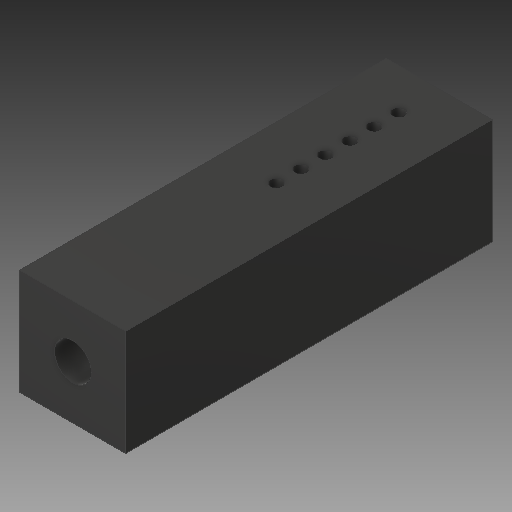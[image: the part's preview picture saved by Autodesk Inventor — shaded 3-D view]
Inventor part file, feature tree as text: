
AUTODESK INVENTOR PART (.ipt)
format: ipt  version: 2019 (Build 230136000, 136)  size: 146,432 bytes
history: native  units: mm
features: sketch x3, hole x2, extrude x1
ambient origin geometry x8: Origin, YZ Plane, XZ Plane, XY Plane, X Axis, Y Axis, Z Axis, Center Point
bodies: Solid1 (feature_tree)
feature tree (6):
  extrude  "Extrusion1"  Depth=13.0mm
  hole  "Hole1"  [1 undecoded]
  hole  "Hole2"  [1 undecoded]
  sketch  "Sketch1"  dims[d0=13.0mm d1=13.0mm]
  sketch  "Sketch2"  dims[d2=45.0mm d3=0.0mm d4=7.5mm]
  sketch  "Sketch3"  dims[d5=6.5mm d6=6.5mm d7=4.5mm d8=6.0mm d9=7.5mm d10=40.5mm d11=90.0deg d12=0.5mm d13=20.594885mm d14=2.0mm d15=6.5mm d16=5.0mm d17=2.0mm d18=3.0mm d19=6.5mm d20=2.0mm d21=3.0mm d22=6.5mm d23=2.0mm d24=3.0mm d25=6.5mm d26=2.0mm d27=3.0mm d28=2.0mm d29=3.0mm d30=6.5mm d31=1.5mm d32=6.0mm d33=7.5mm d34=40.5mm d35=90.0deg d36=0.5mm d37=20.594885mm]
note: 2 required parameter values undecoded (feature->parameter linkage not recoverable at this tier; creation-order binding heuristic only, values carry confidence <= 0.55)
